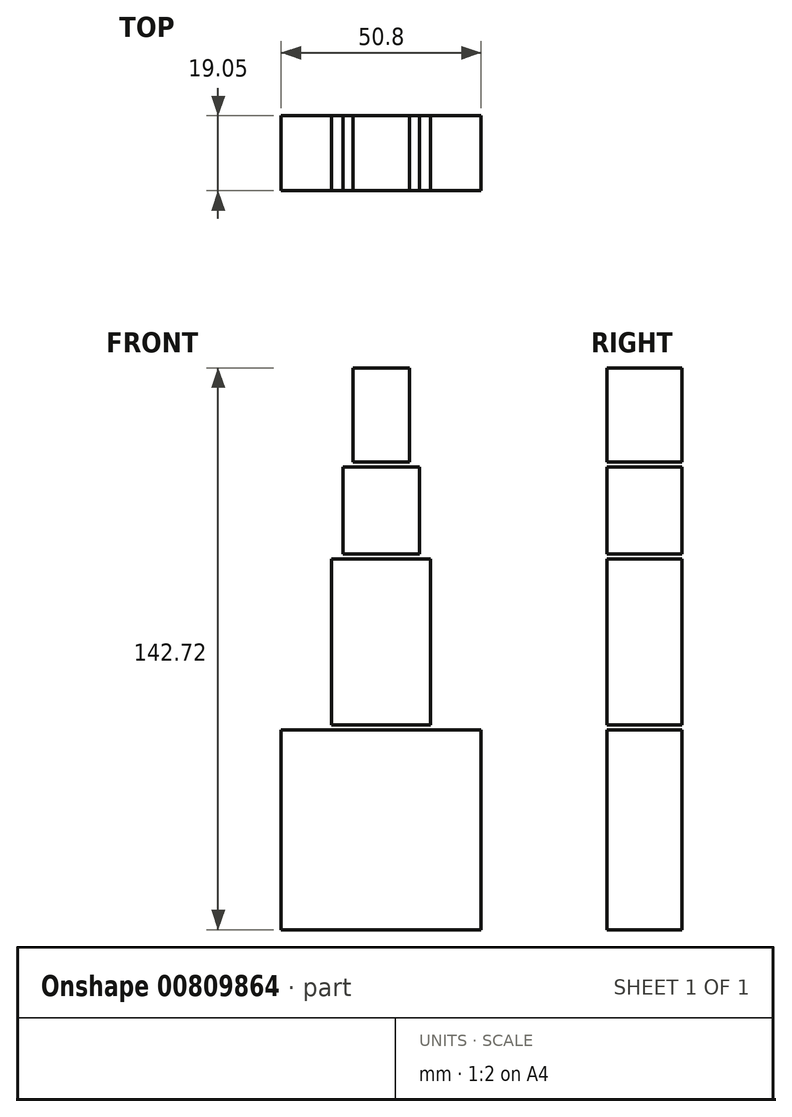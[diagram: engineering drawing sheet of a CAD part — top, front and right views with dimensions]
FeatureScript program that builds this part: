
annotation { "Feature Type Name" : "Feature", "Feature Type Description" : "" }
export const myFeature = defineFeature(function(context is Context, id is Id, definition is map)
    precondition{}
    {
        {
            var Q0;
            Q0=qCreatedBy(makeId("Front.planeOp"),FACE);
            var sketch = newSketch(context, id + "F0", { "sketchPlane" : qUnion([Q0])});
            skLineSegment(sketch, "E0.bottom", {"start": v(0, 0) * mm, "end": v(50.8, 0) * mm});
            skLineSegment(sketch, "E0.top", {"start": v(0, 50.8) * mm, "end": v(50.8, 50.8) * mm});
            skLineSegment(sketch, "E0.left", {"start": v(0, 0) * mm, "end": v(0, 50.8) * mm});
            skLineSegment(sketch, "E0.right", {"start": v(50.8, 0) * mm, "end": v(50.8, 50.8) * mm});
            skLineSegment(sketch, "E1.bottom", {"start": v(12.83, 52.07) * mm, "end": v(37.97, 52.07) * mm});
            skLineSegment(sketch, "E1.top", {"start": v(12.83, 94.2) * mm, "end": v(37.97, 94.2) * mm});
            skLineSegment(sketch, "E1.left", {"start": v(12.83, 52.07) * mm, "end": v(12.83, 94.2) * mm});
            skLineSegment(sketch, "E1.right", {"start": v(37.97, 52.07) * mm, "end": v(37.97, 94.2) * mm});
            skLineSegment(sketch, "E2.bottom", {"start": v(15.67, 95.48) * mm, "end": v(35.13, 95.48) * mm});
            skLineSegment(sketch, "E2.top", {"start": v(15.67, 117.58) * mm, "end": v(35.13, 117.58) * mm});
            skLineSegment(sketch, "E2.left", {"start": v(15.67, 95.48) * mm, "end": v(15.67, 117.58) * mm});
            skLineSegment(sketch, "E2.right", {"start": v(35.13, 95.48) * mm, "end": v(35.13, 117.58) * mm});
            skLineSegment(sketch, "E3.bottom", {"start": v(18.21, 118.85) * mm, "end": v(32.59, 118.85) * mm});
            skLineSegment(sketch, "E3.top", {"start": v(18.21, 142.72) * mm, "end": v(32.59, 142.72) * mm});
            skLineSegment(sketch, "E3.left", {"start": v(18.21, 118.85) * mm, "end": v(18.21, 142.72) * mm});
            skLineSegment(sketch, "E3.right", {"start": v(32.59, 118.85) * mm, "end": v(32.59, 142.72) * mm});
            skPoint(sketch, "E4", {"position": v(25.4, 0) * mm});
            skLineSegment(sketch, "E5", {"start": v(25.4, 0) * mm, "end": v(25.4, 169.26) * mm, "construction": true});
            skPoint(sketch, "E6", {"position": v(25.4, 52.07) * mm});
            skPoint(sketch, "E7.positionSnap0", {"position": v(25.4, 95.48) * mm});
            skPoint(sketch, "E8", {"position": v(25.4, 118.85) * mm});
            skSolve(sketch);
        }
        {
            var Q0;
            Q0 = qSketchRegion(id + "F0", true);
            extrude(context, id + "F1", {"entities" : qUnion([Q0]), "depth" : 19.05 * mm, "offsetDistance" : 25 * mm});
        }
    });
